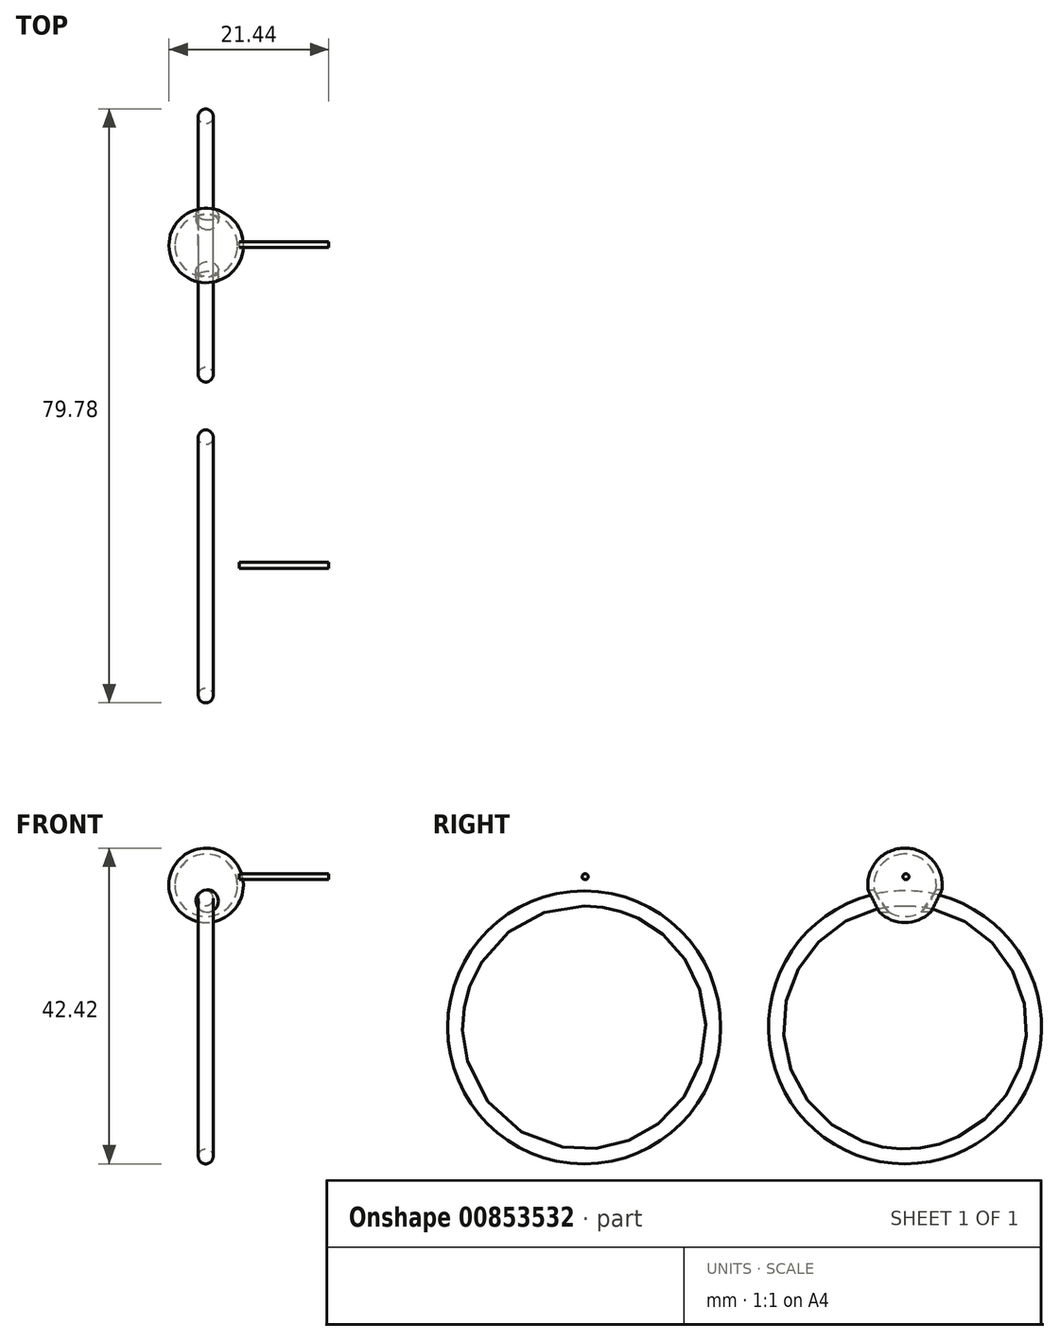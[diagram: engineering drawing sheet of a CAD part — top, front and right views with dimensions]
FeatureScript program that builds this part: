
annotation { "Feature Type Name" : "Feature", "Feature Type Description" : "" }
export const myFeature = defineFeature(function(context is Context, id is Id, definition is map)
    precondition{}
    {
        {
            var Q0;
            Q0=qCreatedBy(makeId("Front.planeOp"),FACE);
            var sketch = newSketch(context, id + "F0", { "sketchPlane" : qUnion([Q0])});
            skArc(sketch, "E0", {"start": v(3.16, 0) * mm, "mid": v(-1.84, 5) * mm, "end": v(-6.84, 0) * mm});
            skLineSegment(sketch, "E1", {"start": v(-6.84, 0) * mm, "end": v(3.16, 0) * mm});
            skArc(sketch, "E2.0", {"start": v(2.36, 0) * mm, "mid": v(-1.84, 4.2) * mm, "end": v(-6.04, 0) * mm});
            skSolve(sketch);
        }
        {
            var Q0;
            Q0=qCreatedBy(makeId("Right.planeOp"),FACE);
            var sketch = newSketch(context, id + "F1", { "sketchPlane" : qUnion([Q0])});
            skCircle(sketch, "E3", {"center": v(0, 0) * mm, "radius": 3.33 * mm});
            skSolve(sketch);
        }
        {
            var Q0;
            {var subQ0=sQuery(id+"F0.wireOp",EDGE,"E0");Q0=makeQuery(id+"F0.imprint","IMPRINT",FACE,{"disambiguationData":[TD([[makeQuery(id+"F0.imprint","IMPRINT",EDGE,{"derivedFrom":subQ0}),1.0]])]});}
            var Q1;
            Q1=sQuery(id+"F1.wireOp",EDGE,"E3");
            revolve(context, id + "F2", {"surfaceOperationType" : NewSurfaceOperationType.NEW, "entities" : qUnion([Q0]), "axis" : qUnion([Q1]), "revolveType" : RevolveType.ONE_DIRECTION, "angle" : 360 * degree});
        }
        {
            var Q0;
            Q0=qCreatedBy(makeId("Front.planeOp"),FACE);
            var sketch = newSketch(context, id + "F3", { "sketchPlane" : qUnion([Q0])});
            skCircle(sketch, "E4", {"center": v(-1.7, -2.1) * mm, "radius": 1.5 * mm});
            skSolve(sketch);
        }
        {
            var Q0;
            Q0 = qSketchRegion(id + "F3", true);
            extrude(context, id + "F4", {"entities" : qUnion([Q0]), "operationType" : NewBodyOperationType.REMOVE, "depth" : 11 * mm, "offsetDistance" : 25 * mm});
        }
        {
            var Q0;
            Q0 = qSketchRegion(id + "F3", true);
            extrude(context, id + "F5", {"entities" : qUnion([Q0]), "operationType" : NewBodyOperationType.REMOVE, "oppositeDirection" : true, "depth" : 25 * mm, "offsetDistance" : 25 * mm});
        }
        {
            var Q0;
            Q0=qCreatedBy(makeId("Right.planeOp"),FACE);
            var sketch = newSketch(context, id + "F6", { "sketchPlane" : qUnion([Q0])});
            skCircle(sketch, "E5", {"center": v(0, -19.39) * mm, "radius": 17.5 * mm});
            skSolve(sketch);
        }
        {
            var Q0;
            Q0=qCreatedBy(makeId("Front.planeOp"),FACE);
            var sketch = newSketch(context, id + "F7", { "sketchPlane" : qUnion([Q0])});
            skCircle(sketch, "E6", {"center": v(0, -36.72) * mm, "radius": 1 * mm});
            skSolve(sketch);
        }
        {
            var Q0;
            Q0=makeQuery(id+"F2.opRevolve","SWEPT_BODY",BODY,{"disambiguationData":[OSD([sQuery(id+"F0.wireOp",EDGE,"E0"),sQuery(id+"F0.wireOp",EDGE,"E1"),sQuery(id+"F0.wireOp",EDGE,"E2.0")])]});
            transform(context, id + "F8", {"entities" : qUnion([Q0]), "transformType" : TransformType.TRANSLATION_3D, "dx" : -16.7 * mm, "dy" : 0 * mm, "dz" : 0 * mm, "makeCopy" : false});
        }
        {
            var Q0;
            Q0=makeQuery(id+"F7.imprint","IMPRINT",FACE,{"disambiguationData":[TD([[makeQuery(id+"F7.imprint","IMPRINT",EDGE,{"derivedFrom":sQuery(id+"F7.wireOp",EDGE,"E6")}),1.0]])]});
            var Q1;
            Q1=sQuery(id+"F6.wireOp",EDGE,"E5");
            revolve(context, id + "F9", {"surfaceOperationType" : NewSurfaceOperationType.NEW, "entities" : qUnion([Q0]), "axis" : qUnion([Q1]), "revolveType" : RevolveType.FULL});
        }
        {
            var Q0;
            Q0=makeQuery(id+"F9.opRevolve","SWEPT_BODY",BODY,{"disambiguationData":[OSD([sQuery(id+"F7.wireOp",EDGE,"E6")])]});
            transform(context, id + "F10", {"entities" : qUnion([Q0]), "transformType" : TransformType.TRANSLATION_3D, "dx" : -18.6 * mm, "dy" : 0 * mm, "dz" : 0.3 * mm, "makeCopy" : false});
        }
        {
            var Q0;
            Q0=qCreatedBy(makeId("Right.planeOp"),FACE);
            var sketch = newSketch(context, id + "F11", { "sketchPlane" : qUnion([Q0])});
            skCircle(sketch, "E7", {"center": v(-11.07, 2.35) * mm, "radius": 0.4 * mm});
            skSolve(sketch);
        }
        {
            var Q0;
            Q0 = qSketchRegion(id + "F11", true);
            extrude(context, id + "F12", {"entities" : qUnion([Q0]), "depth" : 12 * mm, "offsetDistance" : 25 * mm});
        }
        {
            var Q0;
            Q0=makeQuery(id+"F12.opExtrude","SWEPT_BODY",BODY,{"disambiguationData":[OSD([sQuery(id+"F11.wireOp",EDGE,"E7")])]});
            transform(context, id + "F13", {"entities" : qUnion([Q0]), "transformType" : TransformType.TRANSLATION_3D, "dx" : -14.1 * mm, "dy" : 11.2 * mm, "dz" : -1.2 * mm, "makeCopy" : false});
        }
        {
            var Q0;
            Q0=makeQuery(id+"F12.opExtrude","SWEPT_BODY",BODY,{"disambiguationData":[OSD([sQuery(id+"F11.wireOp",EDGE,"E7")])]});
            var Q1;
            Q1=makeQuery(id+"F9.opRevolve","SWEPT_BODY",BODY,{"disambiguationData":[OSD([sQuery(id+"F7.wireOp",EDGE,"E6")])]});
            transform(context, id + "F14", {"entities" : qUnion([Q0, Q1]), "transformType" : TransformType.COPY});
        }
        {
            var Q0;
            Q0=makeQuery(id+"F12.opExtrude","SWEPT_BODY",BODY,{"disambiguationData":[OSD([sQuery(id+"F11.wireOp",EDGE,"E7")])]});
            var Q1;
            Q1=makeQuery(id+"F9.opRevolve","SWEPT_BODY",BODY,{"disambiguationData":[OSD([sQuery(id+"F7.wireOp",EDGE,"E6")])]});
            transform(context, id + "F15", {"entities" : qUnion([Q0, Q1]), "transformType" : TransformType.TRANSLATION_3D, "dx" : 0 * mm, "dy" : -43.1 * mm, "dz" : 0 * mm, "makeCopy" : false});
        }
    });
